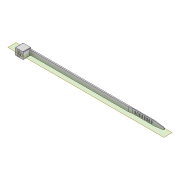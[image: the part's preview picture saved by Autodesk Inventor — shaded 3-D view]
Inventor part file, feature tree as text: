
AUTODESK INVENTOR PART (.ipt)
format: ipt  version: 2022 (Build 260153000, 153)  size: 372,736 bytes
history: native  units: in
note: dims shown in document units (in); Inventor stores cm internally (conversion verified against a paired STEP export)
features: other x2, extrude x2, fillet x2, sketch x2, plane x1, projected_geometry x1
ambient origin geometry x8: Origin, YZ Plane, XZ Plane, XY Plane, X Axis, Y Axis, Z Axis, Center Point
bodies: Solid1 (feature_tree)
feature tree (10):
  other  "Cable_Tie1"
  other  "MeshFeature1"
  extrude  "Extrusion1"  Depth=0.0079in
  fillet  "Fillet1"  Radius=3.937in
  fillet  "Fillet2"  Radius=0.0984in
  plane  "Work Plane1"
  extrude  "Extrusion2"  [1 undecoded]
  sketch  "Sketch1"  dims[d0=0.0709in d1=0.0in d2=0.0079in d3=3.937in d4=0.0984in d5=0.0in]
  sketch  "Sketch2"
  projected_geometry  "Projected Loop1"
note: 1 required parameter value undecoded (feature->parameter linkage not recoverable at this tier; creation-order binding heuristic only, values carry confidence <= 0.55)
